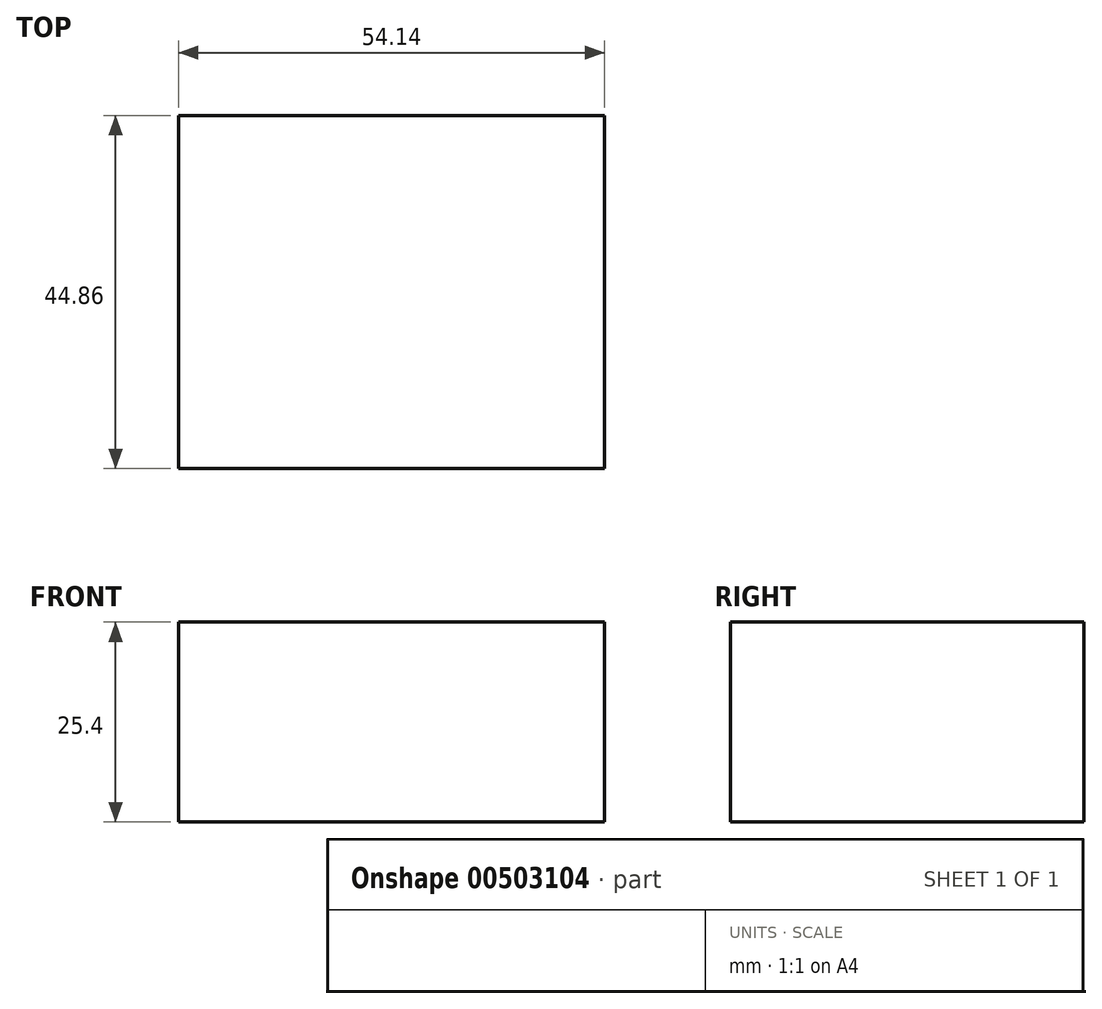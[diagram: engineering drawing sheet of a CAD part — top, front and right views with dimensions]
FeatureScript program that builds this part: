
annotation { "Feature Type Name" : "Feature", "Feature Type Description" : "" }
export const myFeature = defineFeature(function(context is Context, id is Id, definition is map)
    precondition{}
    {
        {
            var Q0;
            Q0=qCreatedBy(makeId("Top.planeOp"),FACE);
            var sketch = newSketch(context, id + "F0", { "sketchPlane" : qUnion([Q0])});
            skLineSegment(sketch, "E0.bottom", {"start": v(-37.78, 44.86) * mm, "end": v(16.36, 44.86) * mm});
            skLineSegment(sketch, "E0.top", {"start": v(-37.78, 0) * mm, "end": v(16.36, 0) * mm});
            skLineSegment(sketch, "E0.left", {"start": v(-37.78, 44.86) * mm, "end": v(-37.78, 0) * mm});
            skLineSegment(sketch, "E0.right", {"start": v(16.36, 44.86) * mm, "end": v(16.36, 0) * mm});
            skSolve(sketch);
        }
        {
            var Q0;
            Q0 = qSketchRegion(id + "F0", true);
            extrude(context, id + "F1", {"entities" : qUnion([Q0]), "depth" : 25.4 * mm});
        }
    });
